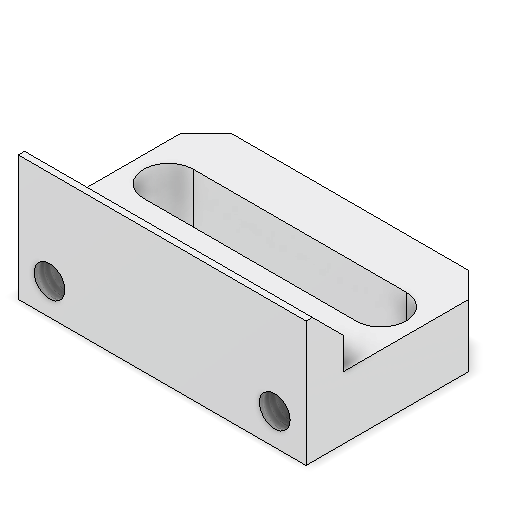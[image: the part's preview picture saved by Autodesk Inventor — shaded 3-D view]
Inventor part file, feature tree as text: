
AUTODESK INVENTOR PART (.ipt)
format: ipt  version: 2025.1 (Build 291241020, 241B)  size: 178,688 bytes
history: native  units: mm
features: sketch x4, extrude x3, chamfer x2, other x1, hole x1
ambient origin geometry x8: Origin, YZ Plane, XZ Plane, XY Plane, X Axis, Y Axis, Z Axis, Center Point
bodies: Body1 (feature_tree)
feature tree (11):
  other  "Sólido1"
  extrude  "Extrusão1"  Depth=23.0mm
  chamfer  "Chanfro1"  Distance=15.0mm
  extrude  "Extrusão3"  Depth=2.0mm TaperAngle=45.0deg
  hole  "Furo1"  [1 undecoded]
  extrude  "Extrusão4"  TaperAngle=0.0deg  [1 undecoded]
  chamfer  "Chanfro2"  Distance=5.0mm
  sketch  "Esboço1"  dims[d0=10.0mm d1=23.0mm d2=15.0mm d3=0.0mm]
  sketch  "Esboço2"  dims[d5=2.459mm d6=5.0mm d7=6.5mm d8=3.4mm d9=90.0deg d10=7.5mm d11=20.594885mm d12=2.0mm d13=2.0mm d14=45.0deg]
  sketch  "Esboço4"  dims[d18=6.0mm d19=4.0mm]
  sketch  "Esboço5"  dims[d20=3.0mm d21=0.0mm d22=0.0mm d27=5.0mm d29=3.0mm d30=0.0mm d31=0.0mm d32=2.5mm d33=2.5mm d34=2.0mm d35=45.0deg d36=2.5mm]
note: 2 required parameter values undecoded (feature->parameter linkage not recoverable at this tier; creation-order binding heuristic only, values carry confidence <= 0.55)
